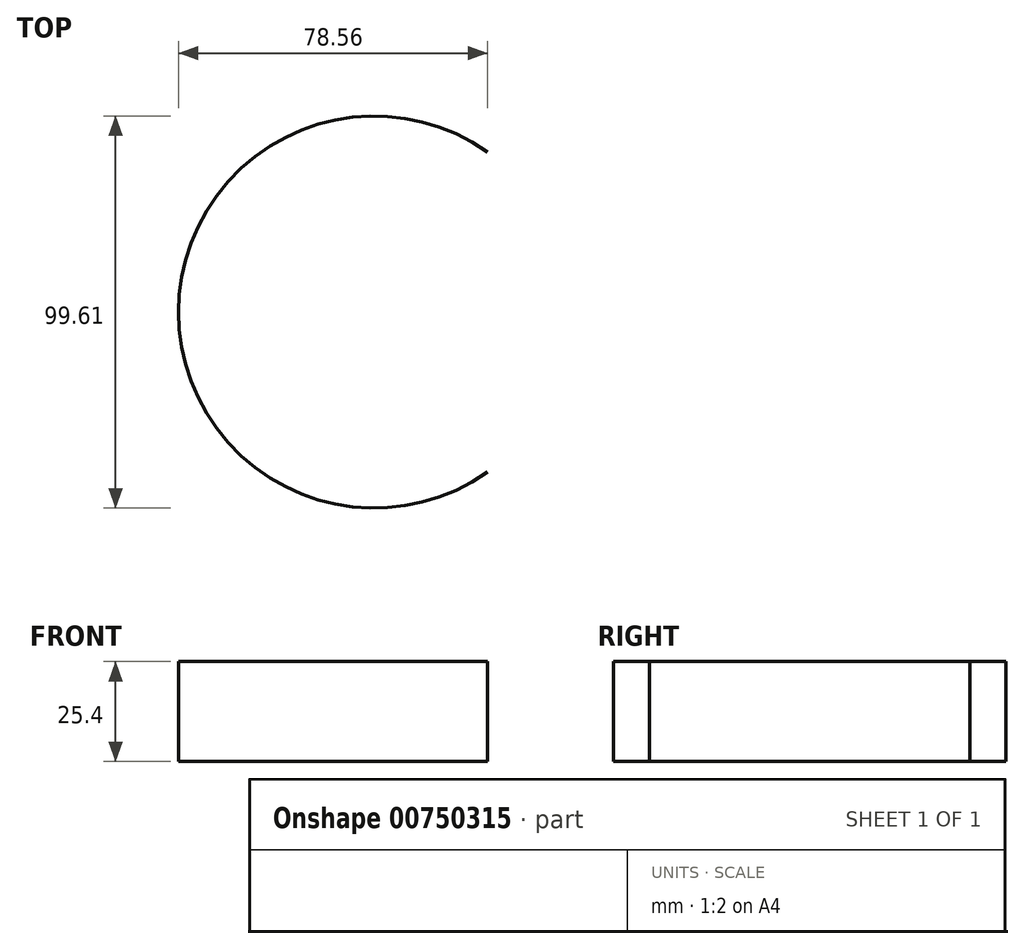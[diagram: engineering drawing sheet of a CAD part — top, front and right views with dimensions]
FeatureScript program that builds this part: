
annotation { "Feature Type Name" : "Feature", "Feature Type Description" : "" }
export const myFeature = defineFeature(function(context is Context, id is Id, definition is map)
    precondition{}
    {
        {
            var Q0;
            Q0=qCreatedBy(makeId("Top.planeOp"),FACE);
            var sketch = newSketch(context, id + "F0", { "sketchPlane" : qUnion([Q0])});
            skArc(sketch, "E0", {"start": v(0, 51.13) * mm, "mid": v(-78.56, 10.47) * mm, "end": v(0, -30.2) * mm});
            skSolve(sketch);
        }
        {
            var Q0;
            Q0=sQuery(id+"F0.wireOp",EDGE,"E0");
            extrude(context, id + "F1", {"bodyType" : ToolBodyType.SURFACE, "surfaceEntities" : qUnion([Q0]), "endBound" : BoundingType.SYMMETRIC, "depth" : 25.4 * mm, "offsetDistance" : 25.4 * mm});
        }
    });
